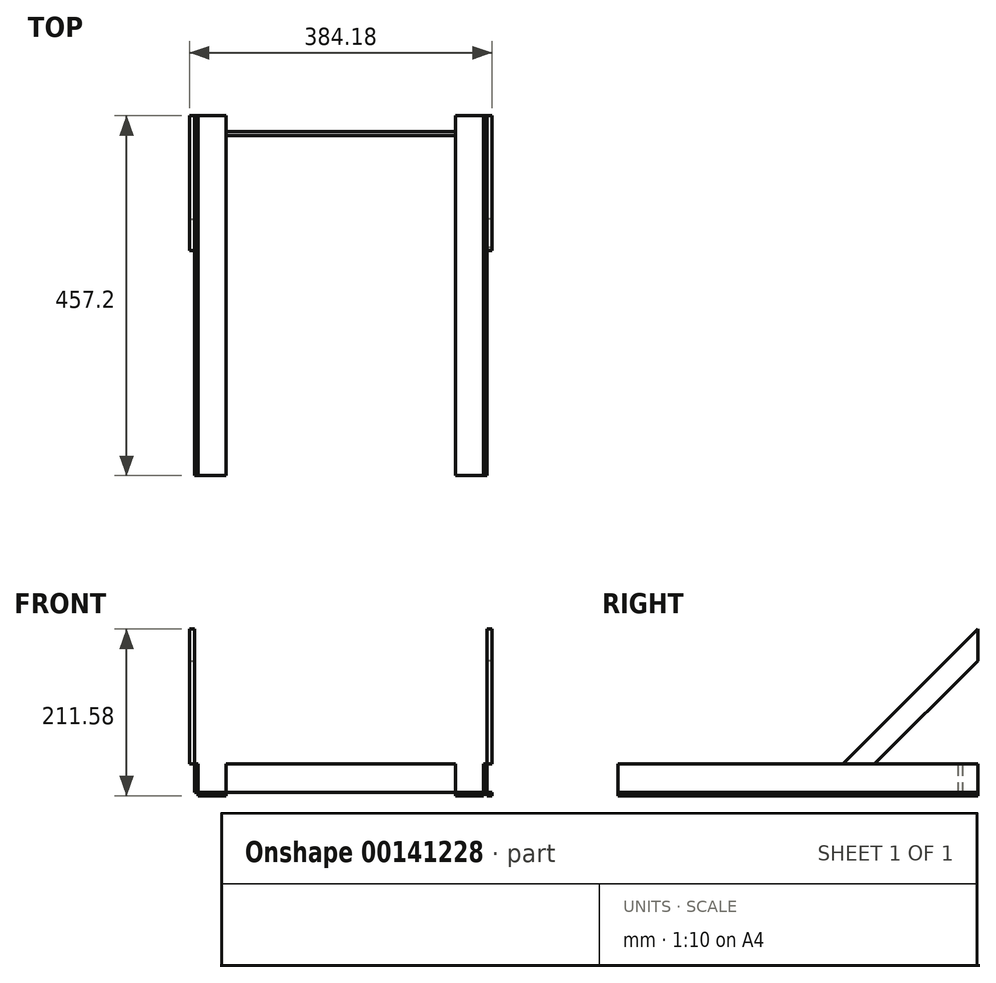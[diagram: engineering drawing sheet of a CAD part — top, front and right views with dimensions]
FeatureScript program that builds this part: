
annotation { "Feature Type Name" : "Feature", "Feature Type Description" : "" }
export const myFeature = defineFeature(function(context is Context, id is Id, definition is map)
    precondition{}
    {
        {
            var Q0;
            Q0=qCreatedBy(makeId("Front.planeOp"),FACE);
            var sketch = newSketch(context, id + "F0", { "sketchPlane" : qUnion([Q0])});
            skLineSegment(sketch, "E0", {"start": v(0, 0) * mm, "end": v(-185.74, 0) * mm, "construction": true});
            skLineSegment(sketch, "E1.bottom", {"start": v(-185.74, 0) * mm, "end": v(-181.55, 0) * mm});
            skLineSegment(sketch, "E1.top", {"start": v(-185.74, -40.13) * mm, "end": v(-181.55, -40.13) * mm});
            skLineSegment(sketch, "E1.left", {"start": v(-185.74, 0) * mm, "end": v(-185.74, -40.13) * mm});
            skLineSegment(sketch, "E1.right", {"start": v(-181.55, 0) * mm, "end": v(-181.55, -40.13) * mm});
            skLineSegment(sketch, "E2.bottom", {"start": v(-185.74, -40.13) * mm, "end": v(-145.86, -40.13) * mm});
            skLineSegment(sketch, "E2.top", {"start": v(-185.74, -35.94) * mm, "end": v(-145.86, -35.94) * mm});
            skLineSegment(sketch, "E2.left", {"start": v(-185.74, -40.13) * mm, "end": v(-185.74, -35.94) * mm});
            skLineSegment(sketch, "E2.right", {"start": v(-145.86, -40.13) * mm, "end": v(-145.86, -35.94) * mm});
            skLineSegment(sketch, "E3", {"start": v(0, 0) * mm, "end": v(0, 28.86) * mm, "construction": true});
            skLineSegment(sketch, "E4.MirrorCS", {"start": v(185.74, 0) * mm, "end": v(181.55, 0) * mm});
            skLineSegment(sketch, "E5.MirrorCS", {"start": v(185.74, -40.13) * mm, "end": v(181.55, -40.13) * mm});
            skLineSegment(sketch, "E6.MirrorCS", {"start": v(145.86, -40.13) * mm, "end": v(145.86, -35.94) * mm});
            skLineSegment(sketch, "E7.MirrorCS", {"start": v(185.74, -40.13) * mm, "end": v(185.74, -35.94) * mm});
            skLineSegment(sketch, "E8.MirrorCS", {"start": v(0, 0) * mm, "end": v(185.74, 0) * mm, "construction": true});
            skLineSegment(sketch, "E9.MirrorCS", {"start": v(185.74, 0) * mm, "end": v(185.74, -40.13) * mm});
            skLineSegment(sketch, "E10.MirrorCS", {"start": v(181.55, 0) * mm, "end": v(181.55, -40.13) * mm});
            skLineSegment(sketch, "E11.MirrorCS", {"start": v(185.74, -40.13) * mm, "end": v(145.86, -40.13) * mm});
            skLineSegment(sketch, "E12.MirrorCS", {"start": v(185.74, -35.94) * mm, "end": v(145.86, -35.94) * mm});
            skSolve(sketch);
        }
        {
            var Q0;
            {var subQ0=sQuery(id+"F0.wireOp",EDGE,"E1.bottom");Q0=makeQuery(id+"F0.imprint","IMPRINT",FACE,{"disambiguationData":[TD([[makeQuery(id+"F0.imprint","IMPRINT",EDGE,{"derivedFrom":subQ0}),-1.0]])]});}
            var Q1;
            {var subQ5=sQuery(id+"F0.wireOp",EDGE,"E2.right");Q1=makeQuery(id+"F0.imprint","IMPRINT",FACE,{"disambiguationData":[TD([[makeQuery(id+"F0.imprint","IMPRINT",EDGE,{"derivedFrom":subQ5}),1.0]])]});}
            var Q2;
            {var subQ5=sQuery(id+"F0.wireOp",EDGE,"E2.left");Q2=makeQuery(id+"F0.imprint","IMPRINT",FACE,{"disambiguationData":[TD([[makeQuery(id+"F0.imprint","IMPRINT",EDGE,{"derivedFrom":subQ5}),-1.0]])]});}
            var Q3;
            {var subQ0=sQuery(id+"F0.wireOp",EDGE,"E4.MirrorCS");Q3=makeQuery(id+"F0.imprint","IMPRINT",FACE,{"disambiguationData":[TD([[makeQuery(id+"F0.imprint","IMPRINT",EDGE,{"derivedFrom":subQ0}),1.0]])]});}
            var Q4;
            {var subQ0=sQuery(id+"F0.wireOp",EDGE,"E11.MirrorCS");var subQ1=sQuery(id+"F0.wireOp",EDGE,"E9.MirrorCS");var subQ2=makeQuery(id+"F0.imprint","INTERSECT",VERTEX,{"derivedFrom":[subQ1,subQ0]});Q4=makeQuery(id+"F0.imprint","IMPRINT",FACE,{"disambiguationData":[TD([[makeQuery(id+"F0.imprint","IMPRINT",EDGE,{"disambiguationData":[TD([[subQ2,1.0]])],"derivedFrom":subQ1}),-1.0]])]});}
            var Q5;
            {var subQ0=sQuery(id+"F0.wireOp",EDGE,"E6.MirrorCS");Q5=makeQuery(id+"F0.imprint","IMPRINT",FACE,{"disambiguationData":[TD([[makeQuery(id+"F0.imprint","IMPRINT",EDGE,{"derivedFrom":subQ0}),-1.0]])]});}
            extrude(context, id + "F1", {"entities" : qUnion([Q0, Q1, Q2, Q3, Q4, Q5]), "endBound" : BoundingType.SYMMETRIC, "oppositeDirection" : true, "depth" : 457.2 * mm});
        }
        {
            var Q0;
            Q0=makeQuery(id+"F1.opExtrude","SWEPT_FACE",FACE,{"disambiguationData":[OSD([sQuery(id+"F0.wireOp",EDGE,"E2.top")])]});
            var sketch = newSketch(context, id + "F2", { "sketchPlane" : qUnion([Q0])});
            skLineSegment(sketch, "E13.0.0", {"start": v(145.86, -228.6) * mm, "end": v(181.55, -228.6) * mm});
            skLineSegment(sketch, "E13.0.1", {"start": v(181.55, -228.6) * mm, "end": v(181.55, 228.6) * mm});
            skLineSegment(sketch, "E13.0.2", {"start": v(181.55, 228.6) * mm, "end": v(145.86, 228.6) * mm});
            skLineSegment(sketch, "E13.0.3", {"start": v(145.86, 228.6) * mm, "end": v(145.86, -228.6) * mm});
            skLineSegment(sketch, "E14.0.0", {"start": v(-181.55, -228.6) * mm, "end": v(-145.86, -228.6) * mm});
            skLineSegment(sketch, "E14.0.1", {"start": v(-145.86, -228.6) * mm, "end": v(-145.86, 228.6) * mm});
            skLineSegment(sketch, "E14.0.2", {"start": v(-145.86, 228.6) * mm, "end": v(-181.55, 228.6) * mm});
            skLineSegment(sketch, "E14.0.3", {"start": v(-181.55, 228.6) * mm, "end": v(-181.55, -228.6) * mm});
            skLineSegment(sketch, "E15", {"start": v(-145.86, -228.6) * mm, "end": v(145.86, -228.6) * mm, "construction": true});
            skLineSegment(sketch, "E16", {"start": v(0, -228.6) * mm, "end": v(0, 203.2) * mm, "construction": true});
            skPoint(sketch, "E16.endSnap0", {"position": v(0, -228.6) * mm});
            skLineSegment(sketch, "E17", {"start": v(181.55, 203.2) * mm, "end": v(-181.55, 203.2) * mm});
            skLineSegment(sketch, "E18", {"start": v(-181.55, 203.2) * mm, "end": v(-181.55, 208.79) * mm});
            skLineSegment(sketch, "E19", {"start": v(-181.55, 208.79) * mm, "end": v(181.55, 208.79) * mm});
            skLineSegment(sketch, "E20", {"start": v(181.55, 208.79) * mm, "end": v(181.55, 203.2) * mm});
            skSolve(sketch);
        }
        {
            var Q0;
            {var subQ5=sQuery(id+"F2.wireOp",EDGE,"E18");Q0=makeQuery(id+"F2.imprint","IMPRINT",FACE,{"disambiguationData":[TD([[makeQuery(id+"F2.imprint","IMPRINT",EDGE,{"derivedFrom":subQ5}),1.0]])]});}
            var Q1;
            {var subQ0=sQuery(id+"F2.wireOp",EDGE,"E19");var subQ1=sQuery(id+"F2.wireOp",EDGE,"E13.0.3");var subQ2=makeQuery(id+"F2.imprint","INTERSECT",VERTEX,{"derivedFrom":[subQ1,subQ0]});Q1=makeQuery(id+"F2.imprint","IMPRINT",FACE,{"disambiguationData":[TD([[makeQuery(id+"F2.imprint","IMPRINT",EDGE,{"disambiguationData":[TD([[subQ2,-1.0]])],"derivedFrom":subQ1}),-1.0]])]});}
            var Q2;
            {var subQ5=sQuery(id+"F2.wireOp",EDGE,"E20");Q2=makeQuery(id+"F2.imprint","IMPRINT",FACE,{"disambiguationData":[TD([[makeQuery(id+"F2.imprint","IMPRINT",EDGE,{"derivedFrom":subQ5}),-1.0]])]});}
            extrude(context, id + "F3", {"entities" : qUnion([Q0, Q1, Q2]), "depth" : 35.94 * mm});
        }
        {
            var Q0;
            Q0=makeQuery(id+"F1.opExtrude","SWEPT_FACE",FACE,{"disambiguationData":[OSD([sQuery(id+"F0.wireOp",EDGE,"E9.MirrorCS")])]});
            var sketch = newSketch(context, id + "F4", { "sketchPlane" : qUnion([Q0])});
            skLineSegment(sketch, "E21", {"start": v(57.15, 0) * mm, "end": v(57.15, -40.13) * mm});
            skLineSegment(sketch, "E22", {"start": v(57.15, 0) * mm, "end": v(228.6, 171.45) * mm});
            skLineSegment(sketch, "E23", {"start": v(228.6, 0) * mm, "end": v(228.6, 202.83) * mm, "construction": true});
            skLineSegment(sketch, "E24", {"start": v(57.15, -40.13) * mm, "end": v(228.6, 131.32) * mm});
            skLineSegment(sketch, "E25", {"start": v(228.6, 171.45) * mm, "end": v(228.6, 131.32) * mm});
            skSolve(sketch);
        }
        {
            var Q0;
            {var subQ0=sQuery(id+"F4.wireOp",EDGE,"E22");Q0=makeQuery(id+"F4.imprint","IMPRINT",FACE,{"disambiguationData":[TD([[makeQuery(id+"F4.imprint","IMPRINT",EDGE,{"derivedFrom":subQ0}),-1.0]])]});}
            var Q1;
            {var subQ0=sQuery(id+"F4.wireOp",EDGE,"E21");Q1=makeQuery(id+"F4.imprint","IMPRINT",FACE,{"disambiguationData":[TD([[makeQuery(id+"F4.imprint","IMPRINT",EDGE,{"derivedFrom":subQ0}),1.0]])]});}
            extrude(context, id + "F5", {"entities" : qUnion([Q0, Q1]), "depth" : 6.35 * mm});
        }
        {
            var Q0;
            Q0=makeQuery(id+"F5.opExtrude","SWEPT_BODY",BODY,{"disambiguationData":[OSD([sQuery(id+"F4.wireOp",EDGE,"E21"),sQuery(id+"F4.wireOp",EDGE,"E22"),sQuery(id+"F4.wireOp",EDGE,"E24"),sQuery(id+"F4.wireOp",EDGE,"E25")])]});
            var Q1;
            Q1=qCreatedBy(makeId("Right.planeOp"),FACE);
            mirror(context, id + "F6", {"operationType" : NewBodyOperationType.ADD, "entities" : qUnion([Q0]), "mirrorPlane" : qUnion([Q1])});
        }
    });
